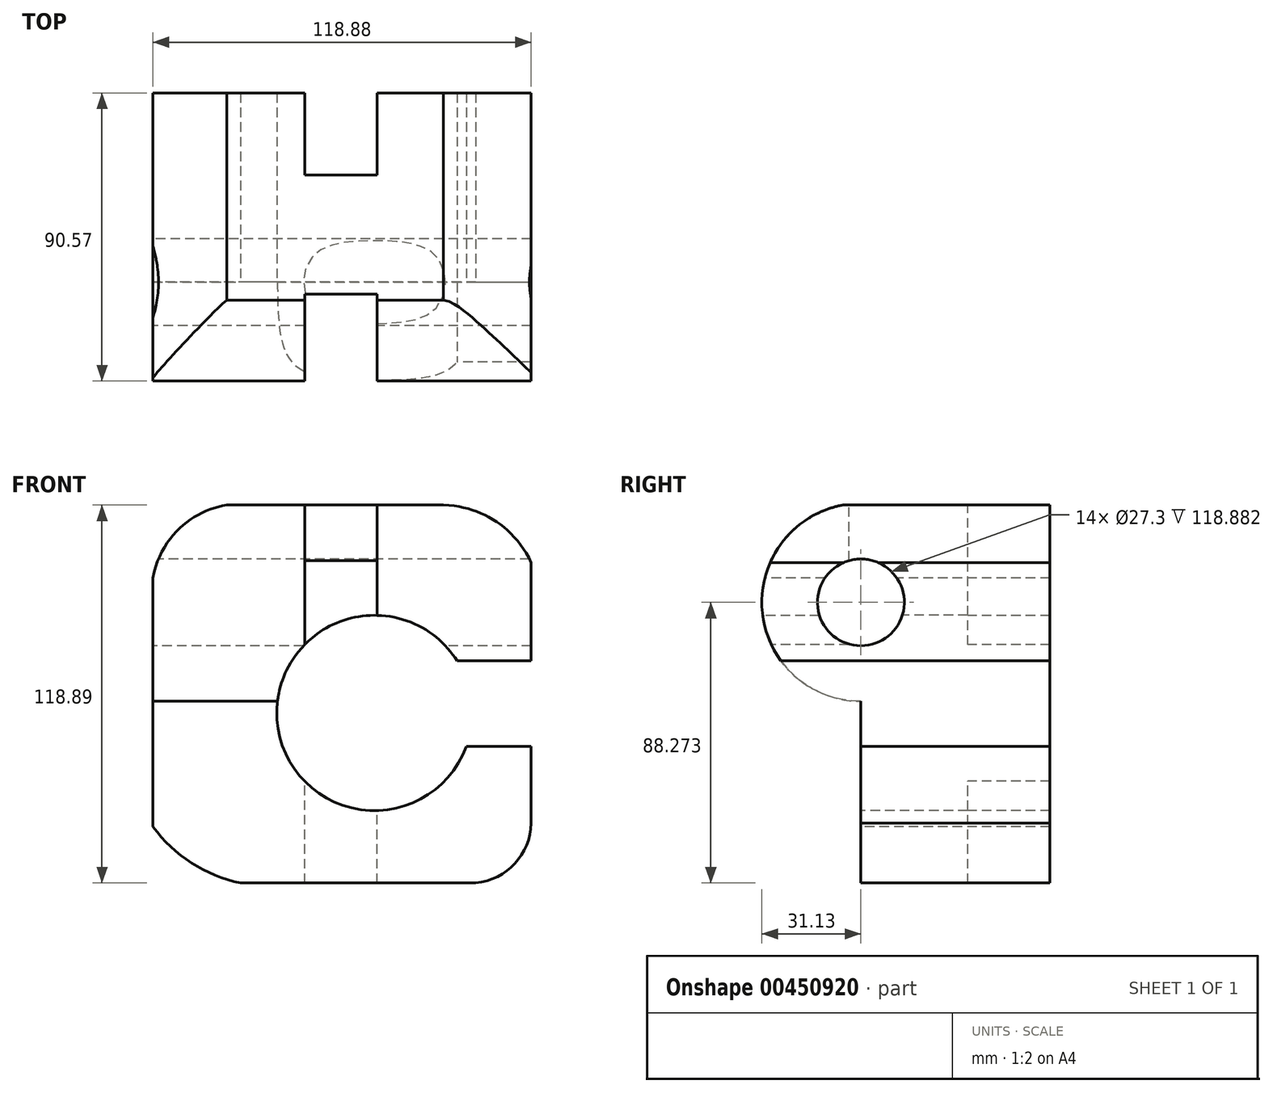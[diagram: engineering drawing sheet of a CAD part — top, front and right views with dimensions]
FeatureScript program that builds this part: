
annotation { "Feature Type Name" : "Feature", "Feature Type Description" : "" }
export const myFeature = defineFeature(function(context is Context, id is Id, definition is map)
    precondition{}
    {
        {
            var Q0;
            Q0=qCreatedBy(makeId("Front.planeOp"),FACE);
            var sketch = newSketch(context, id + "F0", { "sketchPlane" : qUnion([Q0])});
            skLineSegment(sketch, "E0.bottom", {"start": v(59.48, 52.34) * mm, "end": v(-59.4, 52.34) * mm});
            skLineSegment(sketch, "E0.top", {"start": v(59.48, -66.55) * mm, "end": v(-59.4, -66.55) * mm});
            skLineSegment(sketch, "E0.left", {"start": v(59.48, 52.34) * mm, "end": v(59.48, -66.55) * mm});
            skLineSegment(sketch, "E0.right", {"start": v(-59.4, 52.34) * mm, "end": v(-59.4, -66.55) * mm});
            skPoint(sketch, "E0.middle", {"position": v(0.04, -7.1) * mm});
            skSolve(sketch);
        }
        {
            var Q0;
            Q0=makeQuery(id+"F0.imprint","IMPRINT",FACE,{"disambiguationData":[TD([[makeQuery(id+"F0.imprint","IMPRINT",EDGE,{"derivedFrom":sQuery(id+"F0.wireOp",EDGE,"E0.bottom")}),1.0]])]});
            extrude(context, id + "F1", {"entities" : qUnion([Q0]), "depth" : 59.44 * mm, "hasSecondDirection" : true, "secondDirectionOppositeDirection" : true, "secondDirectionDepth" : 59.44 * mm});
        }
        {
            var Q0;
            Q0=makeQuery(id+"F1.opExtrude","CAP_FACE",FACE,{"disambiguationData":[OSD([sQuery(id+"F0.wireOp",EDGE,"E0.bottom"),sQuery(id+"F0.wireOp",EDGE,"E0.top"),sQuery(id+"F0.wireOp",EDGE,"E0.left"),sQuery(id+"F0.wireOp",EDGE,"E0.right")])],"isStart":false});
            var sketch = newSketch(context, id + "F2", { "sketchPlane" : qUnion([Q0])});
            skArc(sketch, "E1", {"start": v(-36.19, 52.34) * mm, "mid": v(-51.47, 44.6) * mm, "end": v(-59.4, 29.42) * mm});
            skArc(sketch, "E2", {"start": v(-59.4, -48.81) * mm, "mid": v(-47.3, -60.23) * mm, "end": v(-31.9, -66.55) * mm});
            skArc(sketch, "E3", {"start": v(38.1, -66.55) * mm, "mid": v(52.9, -61.8) * mm, "end": v(59.48, -47.74) * mm});
            skArc(sketch, "E4", {"start": v(59.48, 34.25) * mm, "mid": v(48.25, 47.24) * mm, "end": v(31.85, 52.34) * mm});
            skLineSegment(sketch, "E5", {"start": v(59.48, 3.35) * mm, "end": v(36.17, 3.35) * mm});
            skLineSegment(sketch, "E6", {"start": v(59.48, -23.63) * mm, "end": v(39.06, -23.63) * mm});
            skArc(sketch, "E7", {"start": v(36.17, 3.35) * mm, "mid": v(-20.33, -16.34) * mm, "end": v(39.06, -23.63) * mm});
            skSolve(sketch);
        }
        {
            var Q0;
            {var subQ0=sQuery(id+"F2.wireOp",EDGE,"E5");Q0=makeQuery(id+"F2.imprint","IMPRINT",FACE,{"disambiguationData":[TD([[makeQuery(id+"F2.imprint","IMPRINT",EDGE,{"derivedFrom":subQ0}),1.0]])]});}
            var Q1;
            {var subQ0=sQuery(id+"F2.wireOp",EDGE,"E1");Q1=makeQuery(id+"F2.imprint","IMPRINT",FACE,{"disambiguationData":[TD([[makeQuery(id+"F2.imprint","IMPRINT",EDGE,{"derivedFrom":subQ0}),-1.0]])]});}
            extrude(context, id + "F3", {"entities" : qUnion([Q0, Q1]), "operationType" : NewBodyOperationType.REMOVE, "endBound" : BoundingType.THROUGH_ALL, "oppositeDirection" : true, "depth" : 31 * mm});
        }
        {
            var Q0;
            {var subQ0=sQuery(id+"F2.wireOp",EDGE,"E4");Q0=makeQuery(id+"F2.imprint","IMPRINT",FACE,{"disambiguationData":[TD([[makeQuery(id+"F2.imprint","IMPRINT",EDGE,{"derivedFrom":subQ0}),-1.0]])]});}
            extrude(context, id + "F4", {"entities" : qUnion([Q0]), "operationType" : NewBodyOperationType.REMOVE, "endBound" : BoundingType.THROUGH_ALL, "oppositeDirection" : true, "depth" : 25 * mm});
        }
        {
            var Q0;
            {var subQ0=sQuery(id+"F2.wireOp",EDGE,"E2");Q0=makeQuery(id+"F2.imprint","IMPRINT",FACE,{"disambiguationData":[TD([[makeQuery(id+"F2.imprint","IMPRINT",EDGE,{"derivedFrom":subQ0}),-1.0]])]});}
            extrude(context, id + "F5", {"entities" : qUnion([Q0]), "operationType" : NewBodyOperationType.REMOVE, "endBound" : BoundingType.THROUGH_ALL, "oppositeDirection" : true, "depth" : 25 * mm});
        }
        {
            var Q0;
            {var subQ0=sQuery(id+"F2.wireOp",EDGE,"E3");var subQ1=makeQuery(id+"F1.opExtrude","CAP_EDGE",EDGE,{"disambiguationData":[OSD([sQuery(id+"F0.wireOp",EDGE,"E0.left")])],"isStart":false});var subQ2=makeQuery(id+"F2.imprint","INTERSECT",VERTEX,{"derivedFrom":[subQ1,subQ0]});Q0=makeQuery(id+"F2.imprint","IMPRINT",FACE,{"disambiguationData":[TD([[makeQuery(id+"F2.imprint","IMPRINT",EDGE,{"disambiguationData":[TD([[subQ2,1.0]])],"derivedFrom":subQ0}),-1.0]])]});}
            extrude(context, id + "F6", {"entities" : qUnion([Q0]), "operationType" : NewBodyOperationType.REMOVE, "endBound" : BoundingType.THROUGH_ALL, "oppositeDirection" : true, "depth" : 25 * mm});
        }
        {
            var Q0;
            Q0=makeQuery(id+"F1.opExtrude","SWEPT_FACE",FACE,{"disambiguationData":[OSD([sQuery(id+"F0.wireOp",EDGE,"E0.right")])]});
            var sketch = newSketch(context, id + "F7", { "sketchPlane" : qUnion([Q0])});
            skLineSegment(sketch, "E8", {"start": v(0, -66.73) * mm, "end": v(0, -9.4) * mm});
            skPoint(sketch, "E8.endSnap0", {"position": v(0, -48.81) * mm});
            skArc(sketch, "E9", {"start": v(0, -9.4) * mm, "mid": v(31.13, 21.72) * mm, "end": v(0, 52.85) * mm});
            skCircle(sketch, "E10", {"center": v(0, 21.72) * mm, "radius": 13.65 * mm});
            skLineSegment(sketch, "E11", {"start": v(0, -66.73) * mm, "end": v(59.77, -66.73) * mm});
            skLineSegment(sketch, "E12", {"start": v(59.77, -66.73) * mm, "end": v(59.44, 52.85) * mm});
            skLineSegment(sketch, "E13", {"start": v(59.44, 52.85) * mm, "end": v(0, 52.85) * mm});
            skSolve(sketch);
        }
        {
            var Q0;
            {var subQ0=sQuery(id+"F0.wireOp",EDGE,"E0.right");var subQ1=makeQuery(id+"F1.opExtrude","CAP_EDGE",EDGE,{"disambiguationData":[OSD([subQ0])],"isStart":false});Q0=makeQuery(id+"F7.imprint","IMPRINT",FACE,{"disambiguationData":[TD([[makeQuery(id+"F7.imprint","IMPRINT",EDGE,{"derivedFrom":subQ1}),-1.0]])]});}
            var Q1;
            {var subQ0=sQuery(id+"F7.wireOp",EDGE,"E11");Q1=makeQuery(id+"F7.imprint","IMPRINT",FACE,{"disambiguationData":[TD([[makeQuery(id+"F7.imprint","IMPRINT",EDGE,{"derivedFrom":subQ0}),1.0]])]});}
            var Q2;
            {var subQ0=sQuery(id+"F7.wireOp",EDGE,"E10");var subQ1=makeQuery(id+"F3.boolean.opBoolean","COPY",EDGE,{"derivedFrom":makeQuery(id+"F3.opExtrude","SWEPT_EDGE",EDGE,{"disambiguationData":[OSD([sQuery(id+"F0.wireOp",EDGE,"E0.right"),sQuery(id+"F2.wireOp",EDGE,"E1")])]})});var subQ2=makeQuery(id+"F7.imprint","INTERSECT",VERTEX,{"disambiguationData":[OD(0.0)],"derivedFrom":[subQ1,subQ0]});Q2=makeQuery(id+"F7.imprint","IMPRINT",FACE,{"disambiguationData":[TD([[makeQuery(id+"F7.imprint","IMPRINT",EDGE,{"disambiguationData":[TD([[subQ2,-1.0]])],"derivedFrom":subQ0}),1.0]])]});}
            var Q3;
            {var subQ0=sQuery(id+"F7.wireOp",EDGE,"E10");var subQ1=makeQuery(id+"F3.boolean.opBoolean","COPY",EDGE,{"derivedFrom":makeQuery(id+"F3.opExtrude","SWEPT_EDGE",EDGE,{"disambiguationData":[OSD([sQuery(id+"F0.wireOp",EDGE,"E0.right"),sQuery(id+"F2.wireOp",EDGE,"E1")])]})});var subQ2=makeQuery(id+"F7.imprint","INTERSECT",VERTEX,{"disambiguationData":[OD(0.0)],"derivedFrom":[subQ1,subQ0]});Q3=makeQuery(id+"F7.imprint","IMPRINT",FACE,{"disambiguationData":[TD([[makeQuery(id+"F7.imprint","IMPRINT",EDGE,{"disambiguationData":[TD([[subQ2,1.0]])],"derivedFrom":subQ0}),1.0]])]});}
            extrude(context, id + "F8", {"entities" : qUnion([Q0, Q1, Q2, Q3]), "operationType" : NewBodyOperationType.REMOVE, "endBound" : BoundingType.THROUGH_ALL, "oppositeDirection" : true, "depth" : 25 * mm});
        }
        {
            var Q0;
            Q0=makeQuery(id+"F1.opExtrude","SWEPT_FACE",FACE,{"disambiguationData":[OSD([sQuery(id+"F0.wireOp",EDGE,"E0.bottom")])]});
            var sketch = newSketch(context, id + "F9", { "sketchPlane" : qUnion([Q0])});
            skLineSegment(sketch, "E14", {"start": v(-64.88, 69.35) * mm, "end": v(-64.88, -48.9) * mm});
            skLineSegment(sketch, "E15", {"start": v(-64.88, -48.9) * mm, "end": v(-11.75, -48.9) * mm});
            skLineSegment(sketch, "E16", {"start": v(-11.75, -48.9) * mm, "end": v(-11.75, -3.76) * mm});
            skLineSegment(sketch, "E17", {"start": v(-11.75, -3.76) * mm, "end": v(11.05, -3.76) * mm});
            skLineSegment(sketch, "E18", {"start": v(11.05, -3.76) * mm, "end": v(11.05, -48.66) * mm});
            skLineSegment(sketch, "E19", {"start": v(11.05, -48.66) * mm, "end": v(66.53, -48.66) * mm});
            skLineSegment(sketch, "E20", {"start": v(66.53, -48.66) * mm, "end": v(66.53, 69.35) * mm});
            skLineSegment(sketch, "E21", {"start": v(66.53, 69.35) * mm, "end": v(11.05, 69.35) * mm});
            skLineSegment(sketch, "E22", {"start": v(11.05, 69.35) * mm, "end": v(11.05, 33.62) * mm});
            skLineSegment(sketch, "E23", {"start": v(11.05, 33.62) * mm, "end": v(-11.75, 33.62) * mm});
            skLineSegment(sketch, "E24", {"start": v(-11.75, 33.62) * mm, "end": v(-11.75, 69.35) * mm});
            skLineSegment(sketch, "E25", {"start": v(-11.75, 69.35) * mm, "end": v(-64.88, 69.35) * mm});
            skLineSegment(sketch, "E26", {"start": v(11.05, -48.66) * mm, "end": v(-11.75, -48.9) * mm});
            skSolve(sketch);
        }
        {
            var Q0;
            {var subQ0=sQuery(id+"F9.wireOp",EDGE,"E23");Q0=makeQuery(id+"F9.imprint","IMPRINT",FACE,{"disambiguationData":[TD([[makeQuery(id+"F9.imprint","IMPRINT",EDGE,{"derivedFrom":subQ0}),-1.0]])]});}
            var Q1;
            {var subQ0=sQuery(id+"F9.wireOp",EDGE,"E17");Q1=makeQuery(id+"F9.imprint","IMPRINT",FACE,{"disambiguationData":[TD([[makeQuery(id+"F9.imprint","IMPRINT",EDGE,{"derivedFrom":subQ0}),-1.0]])]});}
            var Q2;
            {var subQ0=sQuery(id+"F9.wireOp",EDGE,"E26");Q2=makeQuery(id+"F9.imprint","IMPRINT",FACE,{"disambiguationData":[TD([[makeQuery(id+"F9.imprint","IMPRINT",EDGE,{"derivedFrom":subQ0}),-1.0]])]});}
            extrude(context, id + "F10", {"entities" : qUnion([Q0, Q1, Q2]), "operationType" : NewBodyOperationType.REMOVE, "endBound" : BoundingType.THROUGH_ALL, "oppositeDirection" : true, "depth" : 25 * mm});
        }
    });
